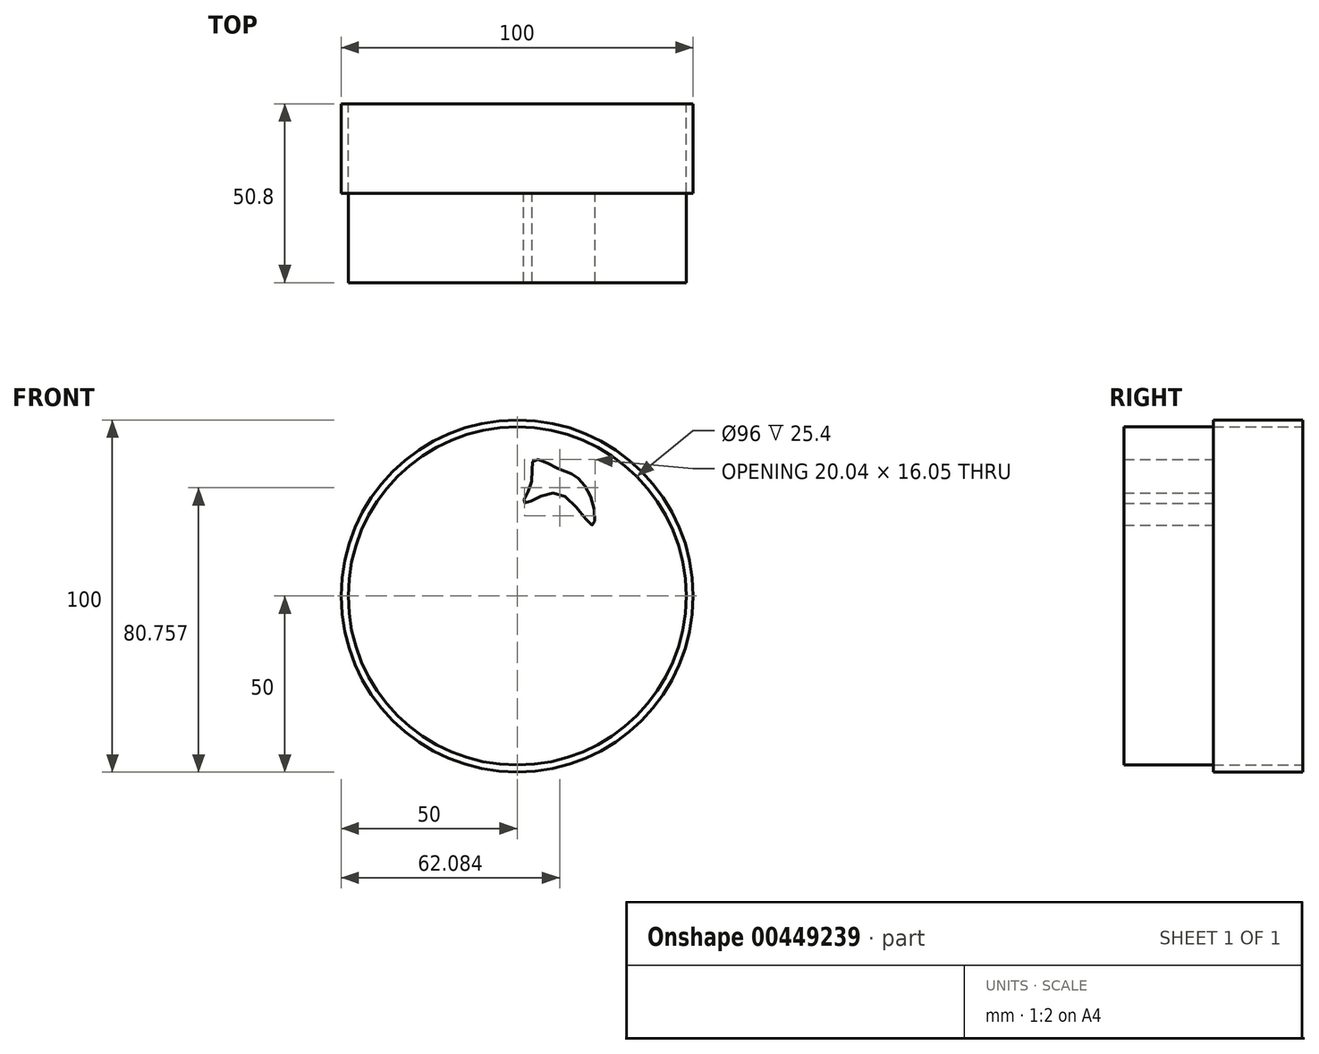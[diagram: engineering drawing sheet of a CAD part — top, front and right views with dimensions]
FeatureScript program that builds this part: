
annotation { "Feature Type Name" : "Feature", "Feature Type Description" : "" }
export const myFeature = defineFeature(function(context is Context, id is Id, definition is map)
    precondition{}
    {
        {
            var Q0;
            Q0=qCreatedBy(makeId("Front.planeOp"),FACE);
            var sketch = newSketch(context, id + "F0", { "sketchPlane" : qUnion([Q0])});
            skCircle(sketch, "E0", {"center": v(0, 0) * mm, "radius": 50 * mm});
            skCircle(sketch, "E1", {"center": v(0, 0) * mm, "radius": 48 * mm});
            skLineSegment(sketch, "E2", {"start": v(0, -40) * mm, "end": v(-29.51, 6.53) * mm});
            skArc(sketch, "E3", {"start": v(0, 15.1) * mm, "mid": v(-20.46, 30.46) * mm, "end": v(-29.51, 6.53) * mm});
            skLineSegment(sketch, "E4", {"start": v(-34.9, 32.94) * mm, "end": v(0, 0) * mm});
            skPoint(sketch, "E5", {"position": v(-27.64, 26.08) * mm});
            skPoint(sketch, "E6", {"position": v(0, -50) * mm});
            skLineSegment(sketch, "E7", {"start": v(-27.64, 26.08) * mm, "end": v(-39.41, 13.6) * mm});
            skLineSegment(sketch, "E8", {"start": v(0, 15.1) * mm, "end": v(0, -40) * mm});
            skLineSegment(sketch, "E9.MirrorCS", {"start": v(0, -40) * mm, "end": v(29.51, 6.53) * mm});
            skArc(sketch, "E10.MirrorCS", {"start": v(0, 15.1) * mm, "mid": v(20.46, 30.46) * mm, "end": v(29.51, 6.53) * mm});
            skArc(sketch, "E11.0", {"start": v(0, 23.35) * mm, "mid": v(24.95, 30.72) * mm, "end": v(31.2, 5.46) * mm});
            skArc(sketch, "E11.1", {"start": v(0, 23.35) * mm, "mid": v(-24.95, 30.72) * mm, "end": v(-31.2, 5.46) * mm});
            skLineSegment(sketch, "E11.2", {"start": v(0, -43.73) * mm, "end": v(-31.2, 5.46) * mm});
            skLineSegment(sketch, "E11.3", {"start": v(0, -43.73) * mm, "end": v(31.2, 5.46) * mm});
            skSolve(sketch);
        }
        {
            var Q0;
            Q0=makeQuery(id+"F0.imprint","IMPRINT",FACE,{"disambiguationData":[TD([[makeQuery(id+"F0.imprint","IMPRINT",EDGE,{"derivedFrom":sQuery(id+"F0.wireOp",EDGE,"E0")}),1.0]])]});
            var Q1;
            {var subQ9=sQuery(id+"F0.wireOp",EDGE,"E2");Q1=makeQuery(id+"F0.imprint","IMPRINT",FACE,{"disambiguationData":[TD([[makeQuery(id+"F0.imprint","IMPRINT",EDGE,{"derivedFrom":subQ9}),1.0]])]});}
            var Q2;
            {var subQ1=sQuery(id+"F0.wireOp",EDGE,"E4");var subQ3=sQuery(id+"F0.wireOp",EDGE,"E11.1");var subQ4=makeQuery(id+"F0.imprint","INTERSECT",VERTEX,{"derivedFrom":[subQ1,subQ3]});Q2=makeQuery(id+"F0.imprint","IMPRINT",FACE,{"disambiguationData":[TD([[makeQuery(id+"F0.imprint","IMPRINT",EDGE,{"disambiguationData":[TD([[subQ4,-1.0]])],"derivedFrom":subQ3}),1.0]])]});}
            extrude(context, id + "F1", {"entities" : qUnion([Q0, Q1, Q2]), "depth" : 25.4 * mm});
        }
        {
            var Q0;
            Q0=makeQuery(id+"F1.opExtrude","SWEPT_EDGE",EDGE,{"disambiguationData":[OSD([sQuery(id+"F0.wireOp",EDGE,"E11.0"),sQuery(id+"F0.wireOp",EDGE,"E11.1")])]});
            fillet(context, id + "F2", {"entities" : qUnion([Q0]), "radius" : 1 * mm, "tangentPropagation" : true, "allowEdgeOverflow" : false});
        }
        {
            var Q0;
            Q0=makeQuery(id+"F1.opExtrude","SWEPT_EDGE",EDGE,{"disambiguationData":[OSD([sQuery(id+"F0.wireOp",EDGE,"E3"),sQuery(id+"F0.wireOp",EDGE,"E8"),sQuery(id+"F0.wireOp",EDGE,"E10.MirrorCS")])]});
            fillet(context, id + "F3", {"entities" : qUnion([Q0]), "radius" : 2 * mm, "tangentPropagation" : true, "allowEdgeOverflow" : false});
        }
        {
            var Q0;
            Q0=makeQuery(id+"F1.opExtrude","SWEPT_EDGE",EDGE,{"disambiguationData":[OSD([sQuery(id+"F0.wireOp",EDGE,"E2"),sQuery(id+"F0.wireOp",EDGE,"E8"),sQuery(id+"F0.wireOp",EDGE,"E9.MirrorCS")])]});
            fillet(context, id + "F4", {"entities" : qUnion([Q0]), "radius" : 1 * mm, "tangentPropagation" : true, "allowEdgeOverflow" : false});
        }
        {
            var Q0;
            Q0=makeQuery(id+"F1.opExtrude","SWEPT_EDGE",EDGE,{"disambiguationData":[OSD([sQuery(id+"F0.wireOp",EDGE,"E11.2"),sQuery(id+"F0.wireOp",EDGE,"E11.3")])]});
            fillet(context, id + "F5", {"entities" : qUnion([Q0]), "radius" : 2 * mm, "tangentPropagation" : true, "allowEdgeOverflow" : false});
        }
        {
            var Q0;
            Q0=makeQuery(id+"F1.opExtrude","SWEPT_BODY",BODY,{"disambiguationData":[OSD([sQuery(id+"F0.wireOp",EDGE,"E2"),sQuery(id+"F0.wireOp",EDGE,"E3"),sQuery(id+"F0.wireOp",EDGE,"E9.MirrorCS"),sQuery(id+"F0.wireOp",EDGE,"E10.MirrorCS"),sQuery(id+"F0.wireOp",EDGE,"E11.0"),sQuery(id+"F0.wireOp",EDGE,"E11.1"),sQuery(id+"F0.wireOp",EDGE,"E11.2"),sQuery(id+"F0.wireOp",EDGE,"E11.3")])]});
            deleteBodies(context, id + "F6", {"entities" : qUnion([Q0])});
        }
        {
            var Q0;
            Q0=makeQuery(id+"F1.opExtrude","CAP_FACE",FACE,{"disambiguationData":[OSD([sQuery(id+"F0.wireOp",EDGE,"E0"),sQuery(id+"F0.wireOp",EDGE,"E1")])],"isStart":false});
            var sketch = newSketch(context, id + "F7", { "sketchPlane" : qUnion([Q0])});
            skArc(sketch, "E12", {"start": v(-7.5, -10) * mm, "mid": v(0, -38) * mm, "end": v(7.5, -10) * mm});
            skPoint(sketch, "E13", {"position": v(0, -38) * mm});
            skArc(sketch, "E14", {"start": v(7.5, 30.5) * mm, "mid": v(0, 38) * mm, "end": v(-7.5, 30.5) * mm});
            skLineSegment(sketch, "E15.left", {"start": v(-7.5, 30.5) * mm, "end": v(-7.5, -10) * mm});
            skLineSegment(sketch, "E15.right", {"start": v(7.5, 30.5) * mm, "end": v(7.5, -10) * mm});
            skPoint(sketch, "E16.orphan", {"position": v(-7.5, -23) * mm});
            skLineSegment(sketch, "E17.0", {"start": v(-9.5, 30.5) * mm, "end": v(-9.5, -8.9) * mm});
            skArc(sketch, "E17.1", {"start": v(9.5, 30.5) * mm, "mid": v(0, 40) * mm, "end": v(-9.5, 30.5) * mm});
            skLineSegment(sketch, "E17.2", {"start": v(9.5, 30.5) * mm, "end": v(9.5, -8.9) * mm});
            skArc(sketch, "E17.3", {"start": v(-9.5, -8.9) * mm, "mid": v(0, -40) * mm, "end": v(9.5, -8.9) * mm});
            skLineSegment(sketch, "E18.0", {"start": v(-5.5, 15) * mm, "end": v(-5.5, -11.22) * mm});
            skArc(sketch, "E18.1", {"start": v(-5.5, -11.22) * mm, "mid": v(0, -36) * mm, "end": v(5.5, -11.22) * mm});
            skLineSegment(sketch, "E18.2", {"start": v(5.5, 15) * mm, "end": v(5.5, -11.22) * mm});
            skLineSegment(sketch, "E19", {"start": v(-5.5, 15) * mm, "end": v(5.5, 15) * mm});
            skLineSegment(sketch, "E20", {"start": v(11.5, 15) * mm, "end": v(26.5, 22.5) * mm});
            skLineSegment(sketch, "E21", {"start": v(26.5, 22.5) * mm, "end": v(26.5, 7.5) * mm});
            skLineSegment(sketch, "E22", {"start": v(26.5, 7.5) * mm, "end": v(11.5, 15) * mm});
            skPoint(sketch, "E23", {"position": v(26.5, 15) * mm});
            skLineSegment(sketch, "E24.0", {"start": v(15.97, 15) * mm, "end": v(24.5, 19.26) * mm});
            skLineSegment(sketch, "E24.1", {"start": v(24.5, 10.74) * mm, "end": v(15.97, 15) * mm});
            skLineSegment(sketch, "E24.2", {"start": v(24.5, 19.26) * mm, "end": v(24.5, 10.74) * mm});
            skSolve(sketch);
        }
        {
            var Q0;
            Q0=qSketchRegion(id+"F7",true);
            var Q1;
            Q1=makeQuery(id+"F7.imprint","IMPRINT",FACE,{"disambiguationData":[TD([[makeQuery(id+"F7.imprint","IMPRINT",EDGE,{"derivedFrom":sQuery(id+"F7.wireOp",EDGE,"E18.0")}),1.0]])]});
            extrude(context, id + "F8", {"entities" : qUnion([Q0, Q1]), "depth" : 25.4 * mm});
        }
        {
            var Q0;
            Q0=makeQuery(id+"F8.opExtrude","SWEPT_EDGE",EDGE,{"disambiguationData":[OSD([sQuery(id+"F7.wireOp",EDGE,"E17.2"),sQuery(id+"F7.wireOp",EDGE,"E17.3")])]});
            var Q1;
            Q1=makeQuery(id+"F8.opExtrude","SWEPT_EDGE",EDGE,{"disambiguationData":[OSD([sQuery(id+"F7.wireOp",EDGE,"E17.0"),sQuery(id+"F7.wireOp",EDGE,"E17.3")])]});
            fillet(context, id + "F9", {"entities" : qUnion([Q0, Q1]), "radius" : 1 * mm, "tangentPropagation" : true, "allowEdgeOverflow" : false});
        }
        {
            var Q0;
            Q0=makeQuery(id+"F8.opExtrude","SWEPT_EDGE",EDGE,{"disambiguationData":[OSD([sQuery(id+"F7.wireOp",EDGE,"E12"),sQuery(id+"F7.wireOp",EDGE,"E15.left")])]});
            var Q1;
            Q1=makeQuery(id+"F8.opExtrude","SWEPT_EDGE",EDGE,{"disambiguationData":[OSD([sQuery(id+"F7.wireOp",EDGE,"E12"),sQuery(id+"F7.wireOp",EDGE,"E15.right")])]});
            fillet(context, id + "F10", {"entities" : qUnion([Q0, Q1]), "radius" : 2 * mm, "tangentPropagation" : true, "allowEdgeOverflow" : false});
        }
        {
            var Q0;
            Q0=makeQuery(id+"F8.opExtrude","SWEPT_EDGE",EDGE,{"disambiguationData":[OSD([sQuery(id+"F7.wireOp",EDGE,"E18.0"),sQuery(id+"F7.wireOp",EDGE,"E18.1")])]});
            var Q1;
            Q1=makeQuery(id+"F8.opExtrude","SWEPT_EDGE",EDGE,{"disambiguationData":[OSD([sQuery(id+"F7.wireOp",EDGE,"E18.1"),sQuery(id+"F7.wireOp",EDGE,"E18.2")])]});
            fillet(context, id + "F11", {"entities" : qUnion([Q0, Q1]), "radius" : 4 * mm, "tangentPropagation" : true, "allowEdgeOverflow" : false});
        }
        {
            var Q0;
            Q0=makeQuery(id+"F8.opExtrude","SWEPT_BODY",BODY,{"disambiguationData":[OSD([sQuery(id+"F7.wireOp",EDGE,"E12"),sQuery(id+"F7.wireOp",EDGE,"E14"),sQuery(id+"F7.wireOp",EDGE,"E15.left"),sQuery(id+"F7.wireOp",EDGE,"E15.right"),sQuery(id+"F7.wireOp",EDGE,"E17.0"),sQuery(id+"F7.wireOp",EDGE,"E17.1"),sQuery(id+"F7.wireOp",EDGE,"E17.2"),sQuery(id+"F7.wireOp",EDGE,"E17.3")])]});
            var Q1;
            Q1=makeQuery(id+"F8.opExtrude","SWEPT_BODY",BODY,{"disambiguationData":[OSD([sQuery(id+"F7.wireOp",EDGE,"E18.0"),sQuery(id+"F7.wireOp",EDGE,"E18.1"),sQuery(id+"F7.wireOp",EDGE,"E18.2"),sQuery(id+"F7.wireOp",EDGE,"E19")])]});
            var Q2;
            Q2=makeQuery(id+"F8.opExtrude","SWEPT_BODY",BODY,{"disambiguationData":[OSD([sQuery(id+"F7.wireOp",EDGE,"E20"),sQuery(id+"F7.wireOp",EDGE,"E21"),sQuery(id+"F7.wireOp",EDGE,"E22"),sQuery(id+"F7.wireOp",EDGE,"E24.0"),sQuery(id+"F7.wireOp",EDGE,"E24.1"),sQuery(id+"F7.wireOp",EDGE,"E24.2")])]});
            deleteBodies(context, id + "F12", {"entities" : qUnion([Q0, Q1, Q2])});
        }
        {
            var Q0;
            Q0=makeQuery(id+"F1.opExtrude","CAP_FACE",FACE,{"disambiguationData":[OSD([sQuery(id+"F0.wireOp",EDGE,"E0"),sQuery(id+"F0.wireOp",EDGE,"E1")])],"isStart":false});
            var sketch = newSketch(context, id + "F13", { "sketchPlane" : qUnion([Q0])});
            skArc(sketch, "E25", {"start": v(-23.5, -6.45) * mm, "mid": v(3.1, -39.8) * mm, "end": v(20.67, -0.93) * mm});
            skLineSegment(sketch, "E26", {"start": v(20.67, -0.93) * mm, "end": v(-6.8, 39.42) * mm});
            skLineSegment(sketch, "E27", {"start": v(-6.8, 39.42) * mm, "end": v(-23.5, -6.45) * mm});
            skPoint(sketch, "E28", {"position": v(0, -40) * mm});
            skLineSegment(sketch, "E29", {"start": v(0, 0) * mm, "end": v(0, 5.34) * mm});
            skArc(sketch, "E30", {"start": v(18.16, 18.85) * mm, "mid": v(26.13, 8.84) * mm, "end": v(31.4, 20.5) * mm});
            skLineSegment(sketch, "E31", {"start": v(18.16, 18.85) * mm, "end": v(23.16, 32.61) * mm});
            skLineSegment(sketch, "E32", {"start": v(23.16, 32.61) * mm, "end": v(31.4, 20.5) * mm});
            skLineSegment(sketch, "E33.0", {"start": v(19.01, -2.06) * mm, "end": v(-6.25, 35.06) * mm});
            skArc(sketch, "E33.1", {"start": v(-21.61, -7.13) * mm, "mid": v(2.85, -37.82) * mm, "end": v(19.01, -2.06) * mm});
            skLineSegment(sketch, "E33.2", {"start": v(-6.25, 35.06) * mm, "end": v(-21.61, -7.13) * mm});
            skLineSegment(sketch, "E34.0", {"start": v(20.04, 18.17) * mm, "end": v(23.7, 28.26) * mm});
            skArc(sketch, "E34.1", {"start": v(20.04, 18.17) * mm, "mid": v(25.89, 10.83) * mm, "end": v(29.75, 19.38) * mm});
            skLineSegment(sketch, "E34.2", {"start": v(23.7, 28.26) * mm, "end": v(29.75, 19.38) * mm});
            skSolve(sketch);
        }
        {
            var Q0;
            Q0=makeQuery(id+"F13.imprint","IMPRINT",FACE,{"disambiguationData":[TD([[makeQuery(id+"F13.imprint","IMPRINT",EDGE,{"derivedFrom":sQuery(id+"F13.wireOp",EDGE,"E25")}),1.0]])]});
            var Q1;
            Q1=makeQuery(id+"F13.imprint","IMPRINT",FACE,{"disambiguationData":[TD([[makeQuery(id+"F13.imprint","IMPRINT",EDGE,{"derivedFrom":sQuery(id+"F13.wireOp",EDGE,"E30")}),1.0]])]});
            extrude(context, id + "F14", {"entities" : qUnion([Q0, Q1]), "depth" : 25.4 * mm});
        }
        {
            var Q0;
            Q0=makeQuery(id+"F14.opExtrude","SWEPT_EDGE",EDGE,{"disambiguationData":[OSD([sQuery(id+"F13.wireOp",EDGE,"E33.0"),sQuery(id+"F13.wireOp",EDGE,"E33.2")])]});
            var Q1;
            Q1=makeQuery(id+"F14.opExtrude","SWEPT_EDGE",EDGE,{"disambiguationData":[OSD([sQuery(id+"F13.wireOp",EDGE,"E34.0"),sQuery(id+"F13.wireOp",EDGE,"E34.2")])]});
            fillet(context, id + "F15", {"entities" : qUnion([Q0, Q1]), "radius" : 1 * mm, "tangentPropagation" : true, "allowEdgeOverflow" : false});
        }
        {
            var Q0;
            Q0=makeQuery(id+"F14.opExtrude","SWEPT_EDGE",EDGE,{"disambiguationData":[OSD([sQuery(id+"F13.wireOp",EDGE,"E26"),sQuery(id+"F13.wireOp",EDGE,"E27")])]});
            var Q1;
            Q1=makeQuery(id+"F14.opExtrude","SWEPT_EDGE",EDGE,{"disambiguationData":[OSD([sQuery(id+"F13.wireOp",EDGE,"E31"),sQuery(id+"F13.wireOp",EDGE,"E32")])]});
            fillet(context, id + "F16", {"entities" : qUnion([Q0, Q1]), "radius" : 2 * mm, "tangentPropagation" : true, "allowEdgeOverflow" : false});
        }
        {
            var Q0;
            Q0=makeQuery(id+"F14.opExtrude","SWEPT_BODY",BODY,{"disambiguationData":[OSD([sQuery(id+"F13.wireOp",EDGE,"E25"),sQuery(id+"F13.wireOp",EDGE,"E26"),sQuery(id+"F13.wireOp",EDGE,"E27"),sQuery(id+"F13.wireOp",EDGE,"E33.0"),sQuery(id+"F13.wireOp",EDGE,"E33.1"),sQuery(id+"F13.wireOp",EDGE,"E33.2")])]});
            var Q1;
            Q1=makeQuery(id+"F14.opExtrude","SWEPT_BODY",BODY,{"disambiguationData":[OSD([sQuery(id+"F13.wireOp",EDGE,"E30"),sQuery(id+"F13.wireOp",EDGE,"E31"),sQuery(id+"F13.wireOp",EDGE,"E32"),sQuery(id+"F13.wireOp",EDGE,"E34.0"),sQuery(id+"F13.wireOp",EDGE,"E34.1"),sQuery(id+"F13.wireOp",EDGE,"E34.2")])]});
            deleteBodies(context, id + "F17", {"entities" : qUnion([Q0, Q1])});
        }
        {
            var Q0;
            Q0=makeQuery(id+"F1.opExtrude","CAP_FACE",FACE,{"disambiguationData":[OSD([sQuery(id+"F0.wireOp",EDGE,"E0"),sQuery(id+"F0.wireOp",EDGE,"E1")])],"isStart":false});
            var sketch = newSketch(context, id + "F18", { "sketchPlane" : qUnion([Q0])});
            skFitSpline(sketch, "E35", {"points": [v(-33.14, -14.43) * mm, v(-36.7, -9.85) * mm, v(-28.29, -4.73) * mm, v(-33.37, 11.9) * mm, v(-29.67, 23.67) * mm, v(-10.74, 15.59) * mm, v(-3.08, 19.76) * mm, v(11.2, 15.82) * mm, v(23.9, 4.04) * mm, v(25.75, -16.05) * mm, v(11.2, -11.43) * mm, v(15.59, -34.06) * mm, v(7.04, -34.3) * mm, v(-9.58, -24.6) * mm, v(-22.89, -30.33) * mm, v(-26.9, -17.2) * mm, v(-33.14, -14.43) * mm]});
            skFitSpline(sketch, "E36.0", {"points": [v(-32.72, -15.4) * mm, v(-33.43, -15.14) * mm, v(-34.12, -14.8) * mm, v(-35.02, -14.28) * mm, v(-36.04, -13.49) * mm, v(-36.85, -12.57) * mm, v(-37.32, -11.78) * mm, v(-37.55, -11.14) * mm, v(-37.64, -10.46) * mm, v(-37.54, -9.87) * mm, v(-37.34, -9.43) * mm, v(-37.07, -9.03) * mm, v(-36.65, -8.62) * mm, v(-36.06, -8.21) * mm, v(-35.4, -7.85) * mm, v(-34.67, -7.52) * mm, v(-33.65, -7.09) * mm, v(-32.32, -6.56) * mm, v(-31.06, -6) * mm, v(-30.2, -5.5) * mm, v(-29.63, -5.12) * mm, v(-29.27, -4.78) * mm, v(-29.04, -4.51) * mm, v(-28.85, -4.24) * mm, v(-28.69, -3.88) * mm, v(-28.58, -3.37) * mm, v(-28.56, -2.79) * mm, v(-28.65, -1.9) * mm, v(-29, -0.63) * mm, v(-29.69, 1.13) * mm, v(-30.58, 3.05) * mm, v(-31.57, 5.1) * mm, v(-32.56, 7.27) * mm, v(-33.31, 9.14) * mm, v(-33.82, 10.67) * mm, v(-34.24, 12.21) * mm, v(-34.59, 14.15) * mm, v(-34.71, 16.41) * mm, v(-34.55, 18.55) * mm, v(-34.09, 20.48) * mm, v(-33.32, 22.15) * mm, v(-32.2, 23.48) * mm, v(-30.96, 24.19) * mm, v(-29.8, 24.44) * mm, v(-28.9, 24.45) * mm, v(-27.96, 24.33) * mm, v(-26.68, 24) * mm, v(-25, 23.36) * mm, v(-22.92, 22.3) * mm, v(-20.77, 21.08) * mm, v(-18.62, 19.8) * mm, v(-16.5, 18.57) * mm, v(-14.5, 17.5) * mm, v(-12.66, 16.71) * mm, v(-11.06, 16.3) * mm, v(-9.84, 16.34) * mm, v(-8.77, 16.72) * mm, v(-7.73, 17.4) * mm, v(-6.68, 18.27) * mm, v(-5.76, 19.06) * mm, v(-4.96, 19.64) * mm, v(-4.3, 20.04) * mm, v(-3.6, 20.39) * mm, v(-2.83, 20.64) * mm, v(-2.03, 20.79) * mm, v(-0.92, 20.87) * mm, v(0.52, 20.77) * mm, v(2.32, 20.4) * mm, v(4.17, 19.84) * mm, v(6.06, 19.11) * mm, v(7.94, 18.28) * mm, v(9.8, 17.38) * mm, v(11.6, 16.46) * mm, v(13.32, 15.55) * mm, v(14.98, 14.62) * mm, v(17.1, 13.3) * mm, v(19.58, 11.38) * mm, v(21.83, 8.9) * mm, v(23.48, 6.43) * mm, v(24.64, 4.3) * mm, v(25.73, 1.9) * mm, v(26.7, -0.71) * mm, v(27.54, -3.42) * mm, v(28.18, -6.12) * mm, v(28.6, -8.72) * mm, v(28.77, -11.13) * mm, v(28.65, -12.9) * mm, v(28.37, -14.16) * mm, v(28.04, -15) * mm, v(27.58, -15.74) * mm, v(26.96, -16.34) * mm, v(26.3, -16.68) * mm, v(25.73, -16.83) * mm, v(25.13, -16.9) * mm, v(24.37, -16.87) * mm, v(23.41, -16.68) * mm, v(22.42, -16.39) * mm, v(21.05, -15.87) * mm, v(19.27, -15.05) * mm, v(17.5, -14.15) * mm, v(16.14, -13.46) * mm, v(15.17, -12.99) * mm, v(14.26, -12.58) * mm, v(13.43, -12.25) * mm, v(12.72, -12.02) * mm, v(12.24, -11.94) * mm, v(11.96, -11.93) * mm, v(11.81, -11.95) * mm, v(11.72, -11.98) * mm, v(11.68, -12) * mm, v(11.66, -12.02) * mm, v(11.61, -12.1) * mm, v(11.56, -12.22) * mm, v(11.5, -12.48) * mm, v(11.47, -12.95) * mm, v(11.53, -13.72) * mm, v(11.68, -14.63) * mm, v(11.91, -15.67) * mm, v(12.22, -16.82) * mm, v(12.7, -18.46) * mm, v(13.4, -20.68) * mm, v(14.32, -23.47) * mm, v(15.2, -26.27) * mm, v(15.92, -28.95) * mm, v(16.32, -30.99) * mm, v(16.46, -32.46) * mm, v(16.45, -33.47) * mm, v(16.3, -34.4) * mm, v(16, -35.22) * mm, v(15.52, -35.9) * mm, v(14.9, -36.42) * mm, v(14.17, -36.75) * mm, v(13.13, -37) * mm, v(11.71, -36.95) * mm, v(9.9, -36.5) * mm, v(8, -35.71) * mm, v(6.1, -34.64) * mm, v(4.29, -33.35) * mm, v(2.52, -31.94) * mm, v(0.78, -30.48) * mm, v(-0.92, -29.06) * mm, v(-2.61, -27.76) * mm, v(-4.29, -26.65) * mm, v(-5.94, -25.82) * mm, v(-7.3, -25.41) * mm, v(-8.4, -25.28) * mm, v(-9.2, -25.29) * mm, v(-10.04, -25.4) * mm, v(-10.9, -25.64) * mm, v(-11.79, -25.97) * mm, v(-12.99, -26.52) * mm, v(-14.5, -27.38) * mm, v(-16.3, -28.52) * mm, v(-18.02, -29.64) * mm, v(-19.37, -30.42) * mm, v(-20.4, -30.9) * mm, v(-21.16, -31.16) * mm, v(-21.91, -31.29) * mm, v(-22.55, -31.25) * mm, v(-23.05, -31.1) * mm, v(-23.4, -30.91) * mm, v(-23.72, -30.68) * mm, v(-24.08, -30.32) * mm, v(-24.45, -29.78) * mm, v(-24.8, -29.04) * mm, v(-25.1, -28.22) * mm, v(-25.42, -27.03) * mm, v(-25.74, -25.38) * mm, v(-26.07, -23.3) * mm, v(-26.4, -21.25) * mm, v(-26.74, -19.7) * mm, v(-27.06, -18.64) * mm, v(-27.28, -18.08) * mm, v(-27.47, -17.7) * mm, v(-27.67, -17.38) * mm, v(-27.94, -17.04) * mm, v(-28.29, -16.73) * mm, v(-28.8, -16.4) * mm, v(-29.59, -16.11) * mm, v(-30.73, -15.87) * mm, v(-31.81, -15.65) * mm, v(-32.72, -15.4) * mm, v(-33.43, -15.14) * mm, v(-34.12, -14.8) * mm, v(-32.72, -15.4) * mm]});
            skFitSpline(sketch, "E37.0", {"points": [v(-32.27, -13.96) * mm, v(-32.85, -13.75) * mm, v(-33.42, -13.48) * mm, v(-34.16, -13.04) * mm, v(-34.85, -12.5) * mm, v(-35.4, -11.94) * mm, v(-35.73, -11.52) * mm, v(-35.96, -11.12) * mm, v(-36.09, -10.76) * mm, v(-36.12, -10.48) * mm, v(-36.09, -10.3) * mm, v(-36.03, -10.18) * mm, v(-35.93, -10.03) * mm, v(-35.7, -9.8) * mm, v(-35.28, -9.5) * mm, v(-34.72, -9.2) * mm, v(-34.07, -8.9) * mm, v(-33.1, -8.48) * mm, v(-31.75, -7.95) * mm, v(-30.4, -7.35) * mm, v(-29.4, -6.79) * mm, v(-28.7, -6.3) * mm, v(-28.2, -5.84) * mm, v(-27.84, -5.42) * mm, v(-27.53, -4.96) * mm, v(-27.25, -4.34) * mm, v(-27.08, -3.54) * mm, v(-27.06, -2.72) * mm, v(-27.18, -1.6) * mm, v(-27.58, -0.13) * mm, v(-28.32, 1.73) * mm, v(-29.23, 3.7) * mm, v(-30.21, 5.75) * mm, v(-31.19, 7.87) * mm, v(-32.05, 10.02) * mm, v(-32.71, 12.18) * mm, v(-33.1, 14.33) * mm, v(-33.2, 16.4) * mm, v(-33.06, 18.32) * mm, v(-32.66, 20) * mm, v(-32.02, 21.36) * mm, v(-31.2, 22.32) * mm, v(-30.4, 22.77) * mm, v(-29.64, 22.94) * mm, v(-29, 22.95) * mm, v(-28.25, 22.86) * mm, v(-27.16, 22.58) * mm, v(-25.63, 22) * mm, v(-23.63, 20.98) * mm, v(-21.53, 19.79) * mm, v(-19.38, 18.51) * mm, v(-17.25, 17.27) * mm, v(-15.16, 16.16) * mm, v(-13.5, 15.44) * mm, v(-12.24, 15.05) * mm, v(-11.32, 14.86) * mm, v(-10.42, 14.8) * mm, v(-9.58, 14.9) * mm, v(-8.8, 15.11) * mm, v(-7.85, 15.52) * mm, v(-6.8, 16.21) * mm, v(-5.7, 17.14) * mm, v(-4.64, 18.04) * mm, v(-3.76, 18.64) * mm, v(-3.03, 19) * mm, v(-2.28, 19.24) * mm, v(-1.19, 19.38) * mm, v(0.3, 19.29) * mm, v(1.94, 18.95) * mm, v(3.68, 18.42) * mm, v(5.48, 17.73) * mm, v(7.3, 16.92) * mm, v(9.13, 16.04) * mm, v(10.91, 15.13) * mm, v(12.6, 14.23) * mm, v(14.22, 13.33) * mm, v(16.24, 12.06) * mm, v(18.56, 10.27) * mm, v(21.06, 7.5) * mm, v(23.32, 3.8) * mm, v(25.02, -0.33) * mm, v(26.09, -3.81) * mm, v(26.71, -6.42) * mm, v(27.12, -8.9) * mm, v(27.27, -11.15) * mm, v(27.16, -12.72) * mm, v(26.93, -13.73) * mm, v(26.69, -14.34) * mm, v(26.4, -14.8) * mm, v(26.07, -15.11) * mm, v(25.76, -15.27) * mm, v(25.46, -15.35) * mm, v(25.1, -15.4) * mm, v(24.56, -15.38) * mm, v(23.52, -15.18) * mm, v(21.98, -14.65) * mm, v(19.94, -13.7) * mm, v(18.18, -12.81) * mm, v(16.8, -12.12) * mm, v(15.8, -11.63) * mm, v(14.85, -11.2) * mm, v(13.95, -10.84) * mm, v(13.1, -10.57) * mm, v(12.44, -10.44) * mm, v(11.92, -10.43) * mm, v(11.53, -10.47) * mm, v(11.15, -10.58) * mm, v(10.78, -10.78) * mm, v(10.48, -11.08) * mm, v(10.26, -11.42) * mm, v(10.12, -11.8) * mm, v(10, -12.3) * mm, v(9.96, -13) * mm, v(10.04, -13.91) * mm, v(10.2, -14.93) * mm, v(10.46, -16.03) * mm, v(10.77, -17.22) * mm, v(11.26, -18.9) * mm, v(11.98, -21.14) * mm, v(12.89, -23.93) * mm, v(13.75, -26.7) * mm, v(14.46, -29.3) * mm, v(14.83, -31.23) * mm, v(14.96, -32.54) * mm, v(14.95, -33.23) * mm, v(14.9, -33.7) * mm, v(14.81, -34.12) * mm, v(14.65, -34.52) * mm, v(14.4, -34.87) * mm, v(14.1, -35.13) * mm, v(13.7, -35.32) * mm, v(13.03, -35.48) * mm, v(11.95, -35.46) * mm, v(10.38, -35.08) * mm, v(8.95, -34.48) * mm, v(7.8, -33.87) * mm, v(6.64, -33.17) * mm, v(5.2, -32.15) * mm, v(3.47, -30.78) * mm, v(1.18, -28.85) * mm, v(-1.13, -26.94) * mm, v(-3.52, -25.36) * mm, v(-5.37, -24.43) * mm, v(-6.97, -23.94) * mm, v(-8.3, -23.78) * mm, v(-9.32, -23.79) * mm, v(-10.35, -23.94) * mm, v(-11.7, -24.3) * mm, v(-13.37, -25.01) * mm, v(-15.29, -26.1) * mm, v(-17.12, -27.27) * mm, v(-18.82, -28.37) * mm, v(-20.09, -29.1) * mm, v(-20.97, -29.5) * mm, v(-21.55, -29.7) * mm, v(-22.02, -29.78) * mm, v(-22.3, -29.75) * mm, v(-22.48, -29.7) * mm, v(-22.64, -29.62) * mm, v(-22.86, -29.44) * mm, v(-23.14, -29.04) * mm, v(-23.4, -28.48) * mm, v(-23.66, -27.78) * mm, v(-23.95, -26.7) * mm, v(-24.26, -25.13) * mm, v(-24.58, -23.07) * mm, v(-24.93, -20.98) * mm, v(-25.28, -19.34) * mm, v(-25.64, -18.16) * mm, v(-25.96, -17.35) * mm, v(-26.36, -16.62) * mm, v(-27, -15.8) * mm, v(-27.96, -15.1) * mm, v(-29.2, -14.66) * mm, v(-30.45, -14.4) * mm, v(-31.48, -14.18) * mm, v(-32.27, -13.96) * mm, v(-32.85, -13.75) * mm, v(-33.42, -13.48) * mm, v(-32.27, -13.96) * mm]});
            skFitSpline(sketch, "E38", {"points": [v(4.07, 32.58) * mm, v(4.85, 38.67) * mm, v(11.97, 36.08) * mm, v(15.84, 34.54) * mm, v(21.05, 27.92) * mm, v(21.43, 20.14) * mm, v(12.23, 28.95) * mm, v(2.9, 26.5) * mm, v(1.87, 26.75) * mm, v(4.07, 32.58) * mm]});
            skFitSpline(sketch, "E39.0", {"points": [v(2.5, 32.4) * mm, v(2.6, 32.86) * mm, v(2.67, 33.33) * mm, v(2.72, 33.84) * mm, v(2.74, 34.35) * mm, v(2.75, 35.06) * mm, v(2.73, 35.94) * mm, v(2.72, 36.81) * mm, v(2.76, 37.5) * mm, v(2.82, 38.02) * mm, v(2.95, 38.56) * mm, v(3.2, 39.14) * mm, v(3.6, 39.63) * mm, v(4.01, 39.94) * mm, v(4.37, 40.11) * mm, v(4.72, 40.22) * mm, v(5.16, 40.3) * mm, v(5.67, 40.3) * mm, v(6.24, 40.21) * mm, v(6.8, 40.07) * mm, v(7.35, 39.9) * mm, v(8.09, 39.61) * mm, v(9.03, 39.2) * mm, v(10.15, 38.65) * mm, v(11.05, 38.19) * mm, v(11.73, 37.85) * mm, v(12.2, 37.63) * mm, v(12.63, 37.43) * mm, v(13.15, 37.2) * mm, v(13.74, 36.99) * mm, v(14.39, 36.77) * mm, v(15.05, 36.55) * mm, v(15.76, 36.27) * mm, v(16.5, 35.9) * mm, v(17.3, 35.41) * mm, v(18.37, 34.6) * mm, v(19.71, 33.29) * mm, v(20.97, 31.57) * mm, v(21.84, 29.94) * mm, v(22.32, 28.82) * mm, v(22.66, 27.86) * mm, v(22.95, 26.88) * mm, v(23.25, 25.64) * mm, v(23.45, 24.42) * mm, v(23.56, 23.48) * mm, v(23.6, 22.8) * mm, v(23.63, 22.16) * mm, v(23.61, 21.55) * mm, v(23.56, 20.97) * mm, v(23.45, 20.42) * mm, v(23.3, 19.95) * mm, v(23.08, 19.56) * mm, v(22.85, 19.26) * mm, v(22.52, 18.96) * mm, v(22.06, 18.72) * mm, v(21.63, 18.64) * mm, v(21.3, 18.64) * mm, v(20.99, 18.68) * mm, v(20.67, 18.79) * mm, v(20.36, 18.94) * mm, v(20.1, 19.1) * mm, v(19.8, 19.34) * mm, v(19.46, 19.66) * mm, v(19.06, 20.08) * mm, v(18.66, 20.55) * mm, v(18.25, 21.07) * mm, v(17.82, 21.61) * mm, v(17.22, 22.38) * mm, v(16.43, 23.38) * mm, v(15.43, 24.58) * mm, v(14.4, 25.7) * mm, v(13.52, 26.48) * mm, v(12.84, 26.97) * mm, v(12.34, 27.27) * mm, v(11.87, 27.5) * mm, v(11.44, 27.64) * mm, v(10.99, 27.73) * mm, v(10.37, 27.77) * mm, v(9.55, 27.7) * mm, v(8.51, 27.44) * mm, v(7.45, 27.03) * mm, v(6.41, 26.54) * mm, v(5.42, 26.02) * mm, v(4.64, 25.6) * mm, v(4.04, 25.32) * mm, v(3.59, 25.13) * mm, v(3.1, 24.98) * mm, v(2.6, 24.9) * mm, v(2.14, 24.89) * mm, v(1.71, 24.98) * mm, v(1.37, 25.11) * mm, v(1.03, 25.34) * mm, v(0.73, 25.65) * mm, v(0.51, 26.02) * mm, v(0.4, 26.4) * mm, v(0.35, 26.76) * mm, v(0.37, 27.06) * mm, v(0.4, 27.32) * mm, v(0.48, 27.63) * mm, v(0.6, 27.98) * mm, v(0.77, 28.38) * mm, v(0.96, 28.78) * mm, v(1.23, 29.33) * mm, v(1.59, 30.05) * mm, v(1.94, 30.81) * mm, v(2.2, 31.44) * mm, v(2.36, 31.92) * mm, v(2.5, 32.4) * mm, v(2.6, 32.86) * mm, v(2.67, 33.33) * mm, v(2.5, 32.4) * mm]});
            skSolve(sketch);
        }
        {
            var Q0;
            Q0=makeQuery(id+"F18.imprint","IMPRINT",FACE,{"disambiguationData":[TD([[makeQuery(id+"F18.imprint","IMPRINT",EDGE,{"derivedFrom":sQuery(id+"F18.wireOp",EDGE,"E35")}),-1.0]])]});
            var Q1;
            Q1=makeQuery(id+"F18.imprint","IMPRINT",FACE,{"disambiguationData":[TD([[makeQuery(id+"F18.imprint","IMPRINT",EDGE,{"derivedFrom":sQuery(id+"F18.wireOp",EDGE,"E35")}),1.0]])]});
            var Q2;
            Q2=makeQuery(id+"F18.imprint","IMPRINT",FACE,{"disambiguationData":[TD([[makeQuery(id+"F18.imprint","IMPRINT",EDGE,{"derivedFrom":sQuery(id+"F18.wireOp",EDGE,"E38")}),1.0]])]});
            extrude(context, id + "F19", {"entities" : qUnion([Q0, Q1, Q2]), "depth" : 25.4 * mm});
        }
    });
